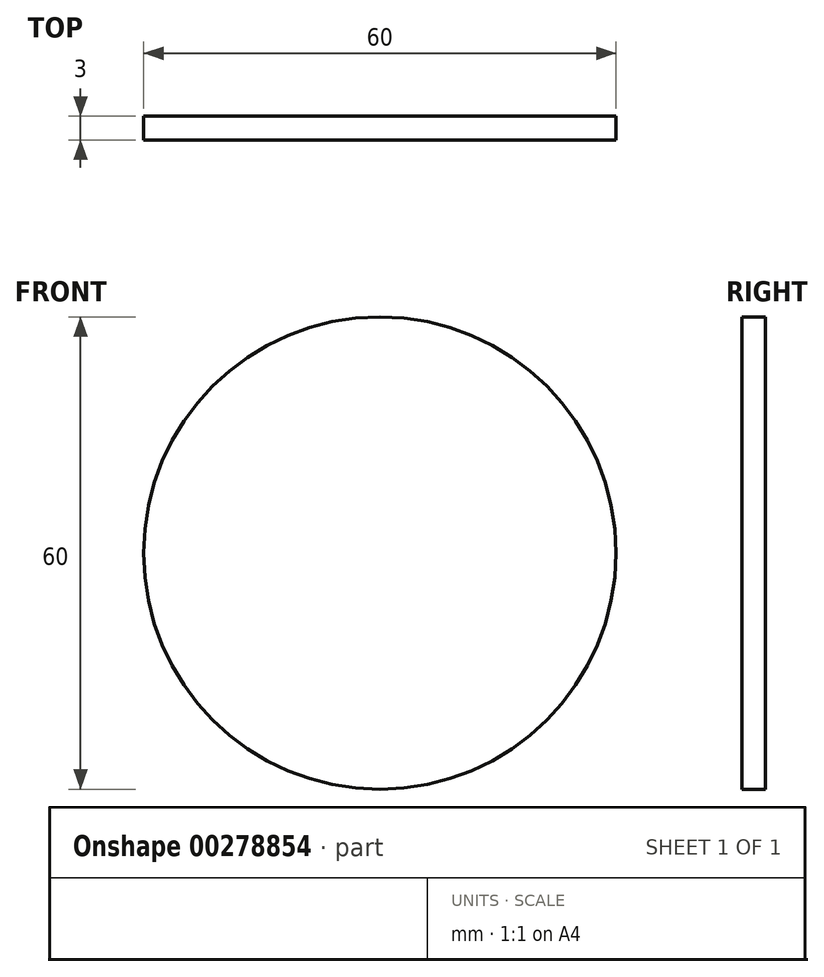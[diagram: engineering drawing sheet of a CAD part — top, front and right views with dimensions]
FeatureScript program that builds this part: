
annotation { "Feature Type Name" : "Feature", "Feature Type Description" : "" }
export const myFeature = defineFeature(function(context is Context, id is Id, definition is map)
    precondition{}
    {
        {
            var Q0;
            Q0=qCreatedBy(makeId("Front.planeOp"),FACE);
            var sketch = newSketch(context, id + "F0", { "sketchPlane" : qUnion([Q0])});
            skCircle(sketch, "E0", {"center": v(0, 0) * mm, "radius": 30 * mm});
            skSolve(sketch);
        }
        {
            var Q0;
            Q0=makeQuery(id+"F0.imprint","IMPRINT",FACE,{"disambiguationData":[TD([[makeQuery(id+"F0.imprint","IMPRINT",EDGE,{"derivedFrom":sQuery(id+"F0.wireOp",EDGE,"E0")}),1.0]])]});
            extrude(context, id + "F1", {"entities" : qUnion([Q0]), "depth" : 3 * mm});
        }
    });
